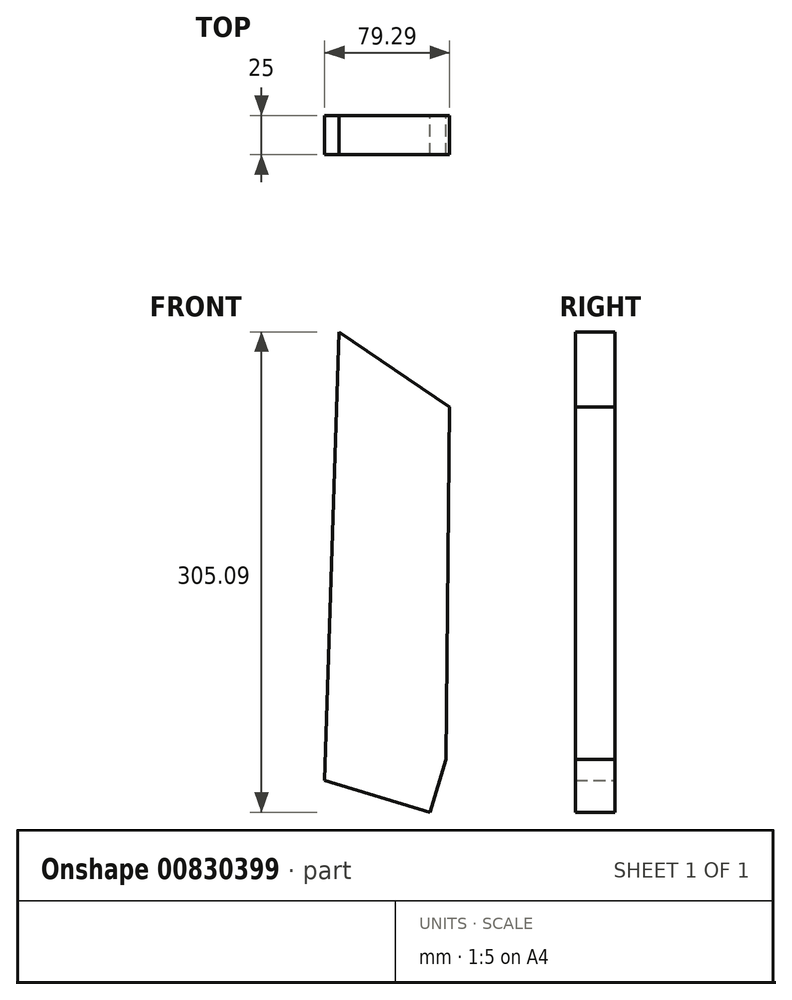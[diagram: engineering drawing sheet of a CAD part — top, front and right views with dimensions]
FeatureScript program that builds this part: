
annotation { "Feature Type Name" : "Feature", "Feature Type Description" : "" }
export const myFeature = defineFeature(function(context is Context, id is Id, definition is map)
    precondition{}
    {
        {
            var Q0;
            Q0=qCreatedBy(makeId("Front.planeOp"),FACE);
            var sketch = newSketch(context, id + "F0", { "sketchPlane" : qUnion([Q0])});
            skLineSegment(sketch, "E0", {"start": v(-343.12, 119.96) * mm, "end": v(-276.1, 99.73) * mm});
            skLineSegment(sketch, "E1", {"start": v(-276.1, 99.73) * mm, "end": v(-266, 133.24) * mm});
            skLineSegment(sketch, "E2", {"start": v(-266, 133.24) * mm, "end": v(-263.83, 357.05) * mm});
            skLineSegment(sketch, "E3", {"start": v(-263.83, 357.05) * mm, "end": v(-334.14, 404.82) * mm});
            skLineSegment(sketch, "E4", {"start": v(-334.14, 404.82) * mm, "end": v(-343.12, 119.96) * mm});
            skLineSegment(sketch, "E5", {"start": v(-343.12, 119.96) * mm, "end": v(-263.83, 357.05) * mm, "construction": true});
            skLineSegment(sketch, "E6", {"start": v(-266, 133.24) * mm, "end": v(-334.14, 404.82) * mm, "construction": true});
            skSolve(sketch);
        }
        {
            var Q0;
            Q0=makeQuery(id+"F0.imprint","IMPRINT",FACE,{"disambiguationData":[TD([[makeQuery(id+"F0.imprint","IMPRINT",EDGE,{"derivedFrom":sQuery(id+"F0.wireOp",EDGE,"E0")}),1.0]])]});
            extrude(context, id + "F1", {"entities" : qUnion([Q0]), "depth" : 25 * mm, "offsetDistance" : 25 * mm});
        }
    });
